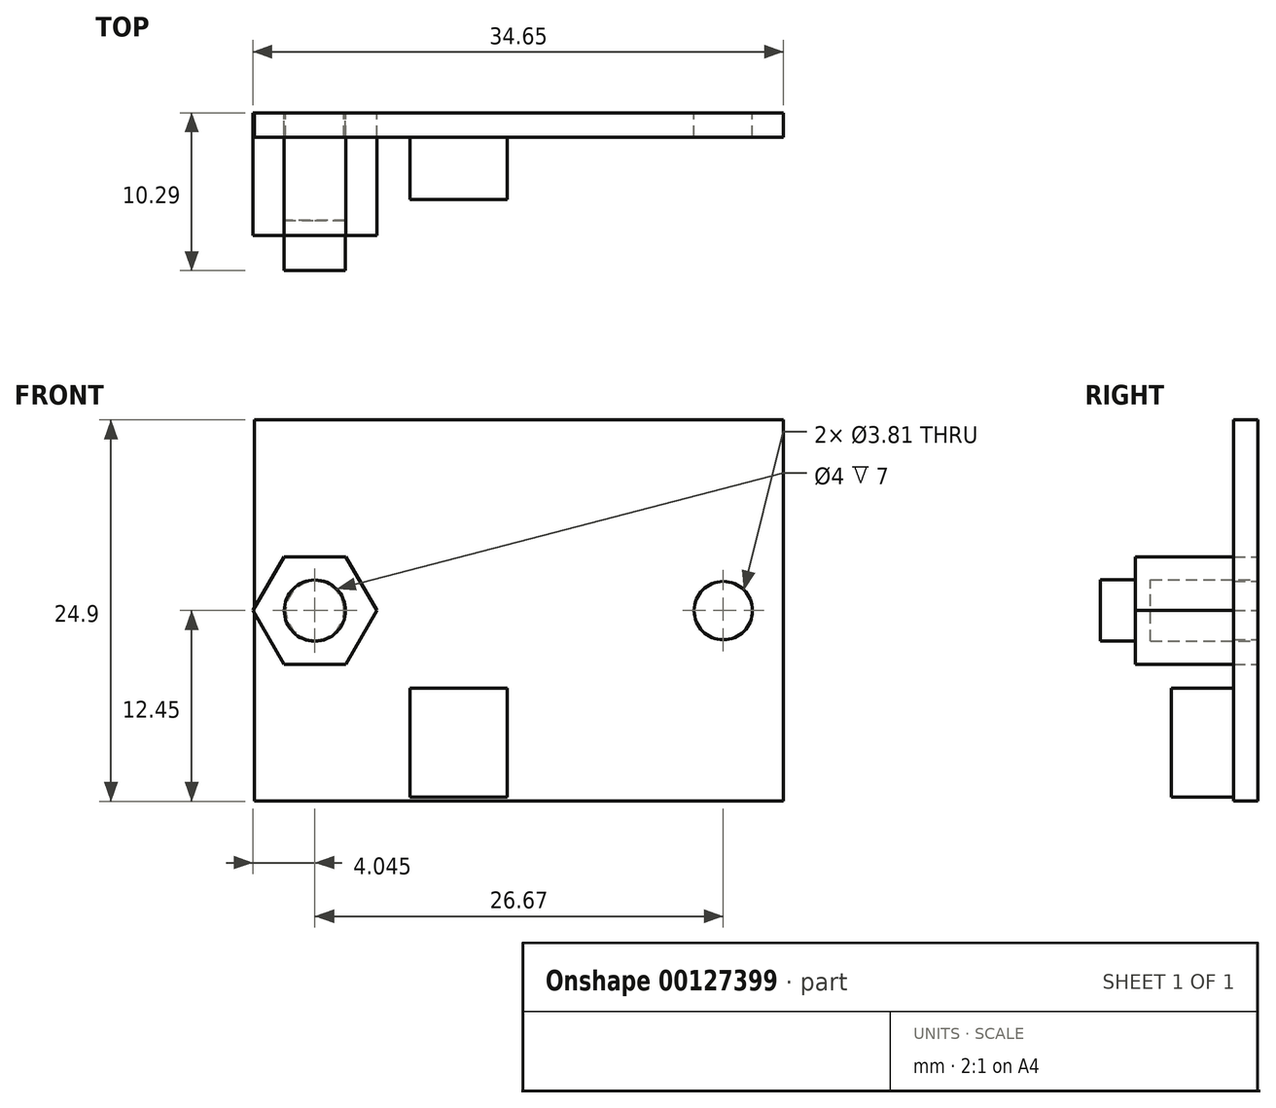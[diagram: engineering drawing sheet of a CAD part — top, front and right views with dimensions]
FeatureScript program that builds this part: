
annotation { "Feature Type Name" : "Feature", "Feature Type Description" : "" }
export const myFeature = defineFeature(function(context is Context, id is Id, definition is map)
    precondition{}
    {
        {
            var Q0;
            Q0=qCreatedBy(makeId("Front.planeOp"),FACE);
            var sketch = newSketch(context, id + "F0", { "sketchPlane" : qUnion([Q0])});
            skLineSegment(sketch, "E0.bottom", {"start": v(17.27, 12.45) * mm, "end": v(-17.27, 12.45) * mm});
            skLineSegment(sketch, "E0.top", {"start": v(17.27, -12.45) * mm, "end": v(-17.27, -12.45) * mm});
            skLineSegment(sketch, "E0.left", {"start": v(17.27, 12.45) * mm, "end": v(17.27, -12.45) * mm});
            skLineSegment(sketch, "E0.right", {"start": v(-17.27, 12.45) * mm, "end": v(-17.27, -12.45) * mm});
            skPoint(sketch, "E0.middle", {"position": v(0, 0) * mm});
            skCircle(sketch, "E1", {"center": v(-13.34, 0) * mm, "radius": 1.9 * mm});
            skCircle(sketch, "E2.MirrorC", {"center": v(13.34, 0) * mm, "radius": 1.9 * mm});
            skSolve(sketch);
        }
        {
            var Q0;
            Q0 = qSketchRegion(id + "F0", true);
            extrude(context, id + "F1", {"entities" : qUnion([Q0]), "depth" : 1.57 * mm});
        }
        {
            var Q0;
            Q0=makeQuery(id+"F1.opExtrude","CAP_FACE",FACE,{"disambiguationData":[OSD([sQuery(id+"F0.wireOp",EDGE,"E0.bottom"),sQuery(id+"F0.wireOp",EDGE,"E0.top"),sQuery(id+"F0.wireOp",EDGE,"E0.left"),sQuery(id+"F0.wireOp",EDGE,"E0.right"),sQuery(id+"F0.wireOp",EDGE,"E1"),sQuery(id+"F0.wireOp",EDGE,"E2.MirrorC")])],"isStart":false});
            var sketch = newSketch(context, id + "F2", { "sketchPlane" : qUnion([Q0])});
            skLineSegment(sketch, "E3.bottom", {"start": v(-0.76, -12.2) * mm, "end": v(-7.11, -12.2) * mm});
            skLineSegment(sketch, "E3.top", {"start": v(-0.76, -5.08) * mm, "end": v(-7.11, -5.08) * mm});
            skLineSegment(sketch, "E3.left", {"start": v(-0.76, -12.2) * mm, "end": v(-0.76, -5.08) * mm});
            skLineSegment(sketch, "E3.right", {"start": v(-7.11, -12.2) * mm, "end": v(-7.11, -5.08) * mm});
            skPoint(sketch, "E3.middle", {"position": v(-3.94, -8.64) * mm});
            skSolve(sketch);
        }
        {
            var Q0;
            Q0 = qSketchRegion(id + "F2", true);
            extrude(context, id + "F3", {"entities" : qUnion([Q0]), "operationType" : NewBodyOperationType.ADD, "depth" : 4.06 * mm});
        }
        {
            var Q0;
            Q0=qCreatedBy(makeId("Front.planeOp"),FACE);
            var sketch = newSketch(context, id + "F4", { "sketchPlane" : qUnion([Q0])});
            skCircle(sketch, "E4.cCircle", {"center": v(-13.33, 0) * mm, "radius": 3.5 * mm, "construction": true});
            skLineSegment(sketch, "E4.0", {"start": v(-9.3, 0) * mm, "end": v(-11.31, -3.5) * mm});
            skLineSegment(sketch, "E4.1", {"start": v(-11.31, -3.5) * mm, "end": v(-15.36, -3.5) * mm});
            skLineSegment(sketch, "E4.2", {"start": v(-15.36, -3.5) * mm, "end": v(-17.38, 0) * mm});
            skLineSegment(sketch, "E4.3", {"start": v(-17.38, 0) * mm, "end": v(-15.36, 3.5) * mm});
            skLineSegment(sketch, "E4.4", {"start": v(-15.36, 3.5) * mm, "end": v(-11.31, 3.5) * mm});
            skLineSegment(sketch, "E4.5", {"start": v(-11.31, 3.5) * mm, "end": v(-9.3, 0) * mm});
            skPoint(sketch, "E4.0.midPoint", {"position": v(-10.3, -1.75) * mm});
            skCircle(sketch, "E5", {"center": v(-13.33, 0) * mm, "radius": 2 * mm});
            skSolve(sketch);
        }
        {
            var Q0;
            Q0=makeQuery(id+"F4.imprint","IMPRINT",FACE,{"disambiguationData":[TD([[makeQuery(id+"F4.imprint","IMPRINT",EDGE,{"derivedFrom":sQuery(id+"F4.wireOp",EDGE,"E4.0")}),-1.0]])]});
            extrude(context, id + "F5", {"entities" : qUnion([Q0]), "depth" : 8 * mm});
        }
        {
            var Q0;
            Q0=makeQuery(id+"F4.imprint","IMPRINT",FACE,{"disambiguationData":[TD([[makeQuery(id+"F4.imprint","IMPRINT",EDGE,{"derivedFrom":sQuery(id+"F4.wireOp",EDGE,"E5")}),1.0]])]});
            extrude(context, id + "F6", {"entities" : qUnion([Q0]), "operationType" : NewBodyOperationType.ADD, "depth" : 10.29 * mm, "hasSecondDirection" : true, "secondDirectionOppositeDirection" : false, "secondDirectionDepth" : 7 * mm});
        }
    });
